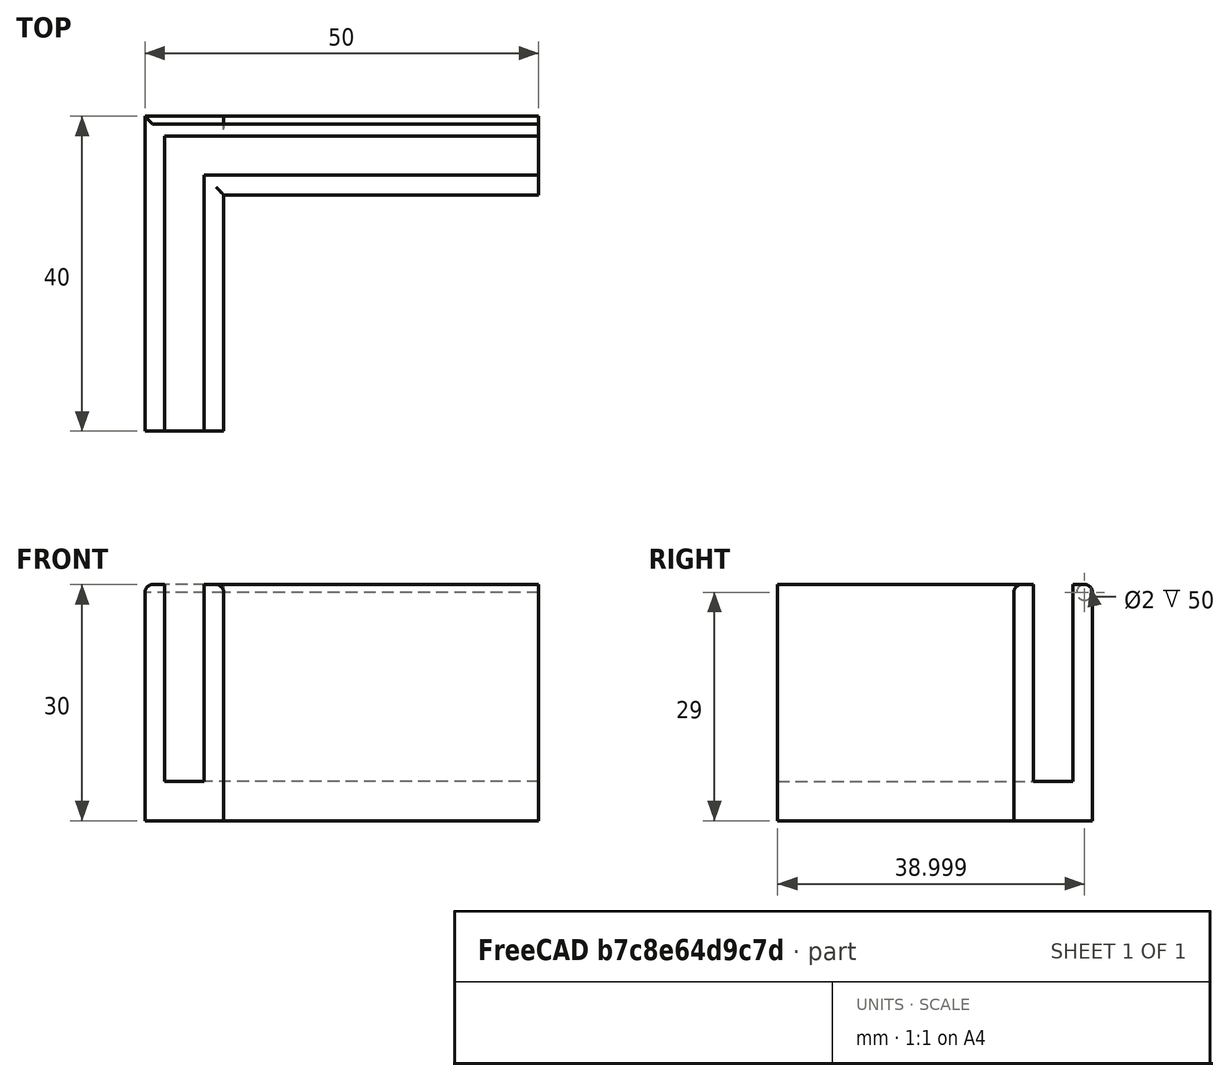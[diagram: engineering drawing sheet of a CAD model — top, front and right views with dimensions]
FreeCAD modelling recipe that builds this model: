
FCSTD DOCUMENT  (FreeCAD 1.1R20251125 (Git shallow))
Label: right angle pliers
License: All rights reserved
LicenseURL: https://en.wikipedia.org/wiki/All_rights_reserved
objects: Sketcher::SketchObject×3, PartDesign::Pocket×2, PartDesign::Fillet×2, App::Point×1, PartDesign::Pad×1, PartDesign::Body×1, Mesh::Feature×1
note: 22 computed .brp shape members not serialized (recipe doc carries the construction recipe); baked Part::Feature solids carry a one-line shape summary decoded from their .brp

FEATURE [App::Point] Origin001
  Role = Origin
FEATURE [Sketcher::SketchObject] Sketch
  ArcFitTolerance = 1e-06
  AttachmentSupport = -> [Origin]
  ExternalTypes = [0]
  FullyConstrained = false
  MakeInternals = false
  MapMode = 5
  sketch-geometry (8):
    g0: LineSegment StartX=-46.9174 StartY=17.6489 StartZ=0 EndX=-6.91741 EndY=17.6489 EndZ=0
    g1: LineSegment StartX=-6.91741 StartY=17.6489 StartZ=0 EndX=-6.91741 EndY=27.6489 EndZ=0
    g2: LineSegment StartX=-6.91741 StartY=27.6489 StartZ=0 EndX=-46.9174 EndY=27.6489 EndZ=0
    g3: LineSegment StartX=-46.9174 StartY=27.6489 StartZ=0 EndX=-56.9174 EndY=27.6489 EndZ=0
    g4: LineSegment StartX=-56.9174 StartY=27.6489 StartZ=0 EndX=-56.9174 EndY=-12.3511 EndZ=0
    g5: LineSegment StartX=-56.9174 StartY=-12.3511 StartZ=0 EndX=-46.9174 EndY=-12.3511 EndZ=0
    g6: LineSegment StartX=-46.9174 StartY=-12.3511 StartZ=0 EndX=-46.9174 EndY=17.6489 EndZ=0
    g7: LineSegment StartX=-46.9174 StartY=27.6489 StartZ=0 EndX=-46.9174 EndY=27.6489 EndZ=0
  constraints (13):
    c: Coincident(g0,g1)
    c: Coincident(g1,g2)
    c: Vertical(g1)
    c: Horizontal(g0)
    c: Horizontal(g2)
    c: DistanceX(g2,g2) = 40
    c: DistanceY(g0,g2) = 10
    c: Coincident(g3,g4)
    c: Coincident(g4,g5)
    c: Coincident(g5,g6)
    c: Coincident(g7,g3)
    c: Coincident(g6,g0)
    c: Coincident(g7,g2)
FEATURE [PartDesign::Pad] Pad
  Direction = (0,0,1)
  Length = 30
  Length2 = 10
  Profile = -> Sketch
  ReferenceAxis = -> Sketch [N_Axis]
  Refine = true
  SideType = 0
  Suppressed = false
  Type = 0
  Type2 = 0
FEATURE [Sketcher::SketchObject] Sketch001
  ArcFitTolerance = 1e-06
  AttachmentSupport = -> [Pad]
  ExternalGeometry = -> [Pad]
  ExternalTypes = [0]
  FullyConstrained = false
  MakeInternals = false
  MapMode = 5
  Placement = pos=(2.2e-15,-12.3511,0) rot=(1,0,0;1.5708rad)
  sketch-geometry (4):
    g0: LineSegment StartX=-54.4174 StartY=37.8612 StartZ=0 EndX=-54.4174 EndY=5 EndZ=0
    g1: LineSegment StartX=-54.4174 StartY=5 StartZ=0 EndX=-49.4174 EndY=5 EndZ=0
    g2: LineSegment StartX=-49.4174 StartY=5 StartZ=0 EndX=-49.4174 EndY=37.8612 EndZ=0
    g3: LineSegment StartX=-49.4174 StartY=37.8612 StartZ=0 EndX=-54.4174 EndY=37.8612 EndZ=0
  constraints (11):
    c: Coincident(g0,g1)
    c: Coincident(g1,g2)
    c: Coincident(g2,g3)
    c: Coincident(g3,g0)
    c: Vertical(g0)
    c: Vertical(g2)
    c: Horizontal(g1)
    c: Horizontal(g3)
    c: DistanceX(g3,g3) = 5
    c: Distance(g-1,g1) = 5
    c: Distance(g-3,g0) = 2.5
FEATURE [PartDesign::Pocket] Pocket
  BaseFeature = -> Pad
  Direction = (0,1,-2e-16)
  Length = 37
  Length2 = 5
  Profile = -> Sketch001
  ReferenceAxis = -> Sketch001 [N_Axis]
  Refine = true
  SideType = 0
  Suppressed = false
  Type = 0
  Type2 = 0
FEATURE [Sketcher::SketchObject] Sketch002
  ArcFitTolerance = 1e-06
  AttachmentSupport = -> [Pocket]
  ExternalGeometry = -> [Pocket]
  ExternalTypes = [0,0]
  FullyConstrained = false
  MakeInternals = false
  MapMode = 5
  Placement = pos=(-6.91741,0,0) rot=(0.57735,0.57735,0.57735;2.0944rad)
  sketch-geometry (4):
    g0: LineSegment StartX=20.1489 StartY=32.8333 StartZ=0 EndX=20.1489 EndY=5 EndZ=0
    g1: LineSegment StartX=20.1489 StartY=5 StartZ=0 EndX=25.1489 EndY=5 EndZ=0
    g2: LineSegment StartX=25.1489 StartY=5 StartZ=0 EndX=25.1489 EndY=32.8333 EndZ=0
    g3: LineSegment StartX=25.1489 StartY=32.8333 StartZ=0 EndX=20.1489 EndY=32.8333 EndZ=0
  constraints (11):
    c: Coincident(g0,g1)
    c: Coincident(g1,g2)
    c: Coincident(g2,g3)
    c: Coincident(g3,g0)
    c: Vertical(g0)
    c: Vertical(g2)
    c: Horizontal(g1)
    c: Horizontal(g3)
    c: DistanceX(g3,g3) = 5
    c: Distance(g-3,g2) = 2.5
    c: Distance(g-4,g1) = 5
FEATURE [PartDesign::Pocket] Pocket001
  BaseFeature = -> Pocket
  Direction = (-1,0,0)
  Length = 47.5
  Length2 = 5
  Profile = -> Sketch002
  ReferenceAxis = -> Sketch002 [N_Axis]
  Refine = true
  SideType = 0
  Suppressed = false
  Type = 0
  Type2 = 0
FEATURE [PartDesign::Fillet] Fillet
  Base = -> Pocket001 [Edge33,Edge32]
  BaseFeature = -> Pocket001
  Radius = 1
  Refine = true
  SupportTransform = false
  Suppressed = false
  UseAllEdges = false
FEATURE [PartDesign::Fillet] Fillet001
  Base = -> Fillet [Edge28,Edge34]
  BaseFeature = -> Fillet
  Radius = 1
  Refine = true
  SupportTransform = false
  Suppressed = false
  UseAllEdges = false
FEATURE [PartDesign::Body] Body
  AllowCompound = true
  Group = -> [Sketch,Pad,Sketch001,Pocket,Sketch002,Pocket001,Fillet,Fillet001]
  Origin = -> Origin
  Tip = -> Fillet001
FEATURE [Mesh::Feature] Mesh  label="Body (Meshed)"
